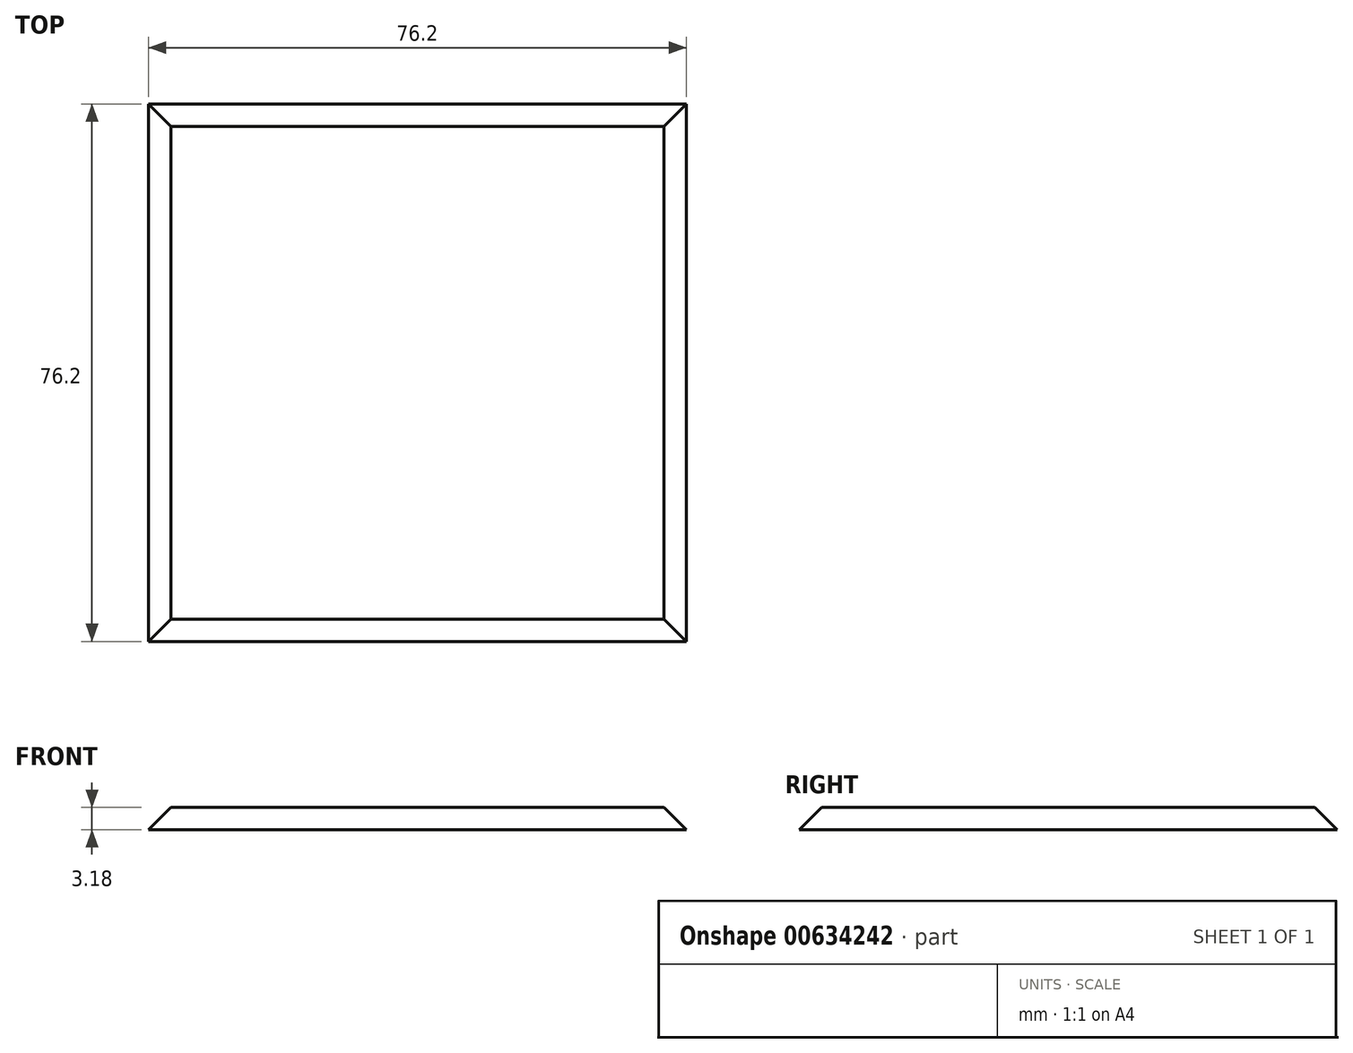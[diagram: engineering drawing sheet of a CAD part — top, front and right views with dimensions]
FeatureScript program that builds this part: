
annotation { "Feature Type Name" : "Feature", "Feature Type Description" : "" }
export const myFeature = defineFeature(function(context is Context, id is Id, definition is map)
    precondition{}
    {
        {
            var Q0;
            Q0=qCreatedBy(makeId("Top.planeOp"),FACE);
            var sketch = newSketch(context, id + "F0", { "sketchPlane" : qUnion([Q0])});
            skLineSegment(sketch, "E0.bottom", {"start": v(0, 0) * mm, "end": v(76.2, 0) * mm});
            skLineSegment(sketch, "E0.top", {"start": v(0, 76.2) * mm, "end": v(76.2, 76.2) * mm});
            skLineSegment(sketch, "E0.left", {"start": v(0, 0) * mm, "end": v(0, 76.2) * mm});
            skLineSegment(sketch, "E0.right", {"start": v(76.2, 0) * mm, "end": v(76.2, 76.2) * mm});
            skSolve(sketch);
        }
        {
            var Q0;
            Q0 = qSketchRegion(id + "F0", true);
            extrude(context, id + "F1", {"entities" : qUnion([Q0]), "depth" : 3.17 * mm, "offsetDistance" : 25.4 * mm});
        }
        {
            var Q0;
            Q0=makeQuery(id+"F1.opExtrude","CAP_EDGE",EDGE,{"disambiguationData":[OSD([sQuery(id+"F0.wireOp",EDGE,"E0.top")])],"isStart":false});
            var Q1;
            Q1=makeQuery(id+"F1.opExtrude","CAP_EDGE",EDGE,{"disambiguationData":[OSD([sQuery(id+"F0.wireOp",EDGE,"E0.right")])],"isStart":false});
            var Q2;
            Q2=makeQuery(id+"F1.opExtrude","CAP_EDGE",EDGE,{"disambiguationData":[OSD([sQuery(id+"F0.wireOp",EDGE,"E0.bottom")])],"isStart":false});
            var Q3;
            Q3=makeQuery(id+"F1.opExtrude","CAP_EDGE",EDGE,{"disambiguationData":[OSD([sQuery(id+"F0.wireOp",EDGE,"E0.left")])],"isStart":false});
            chamfer(context, id + "F2", {"entities" : qUnion([Q0, Q1, Q2, Q3]), "width" : 3.17 * mm, "tangentPropagation" : true});
        }
    });
